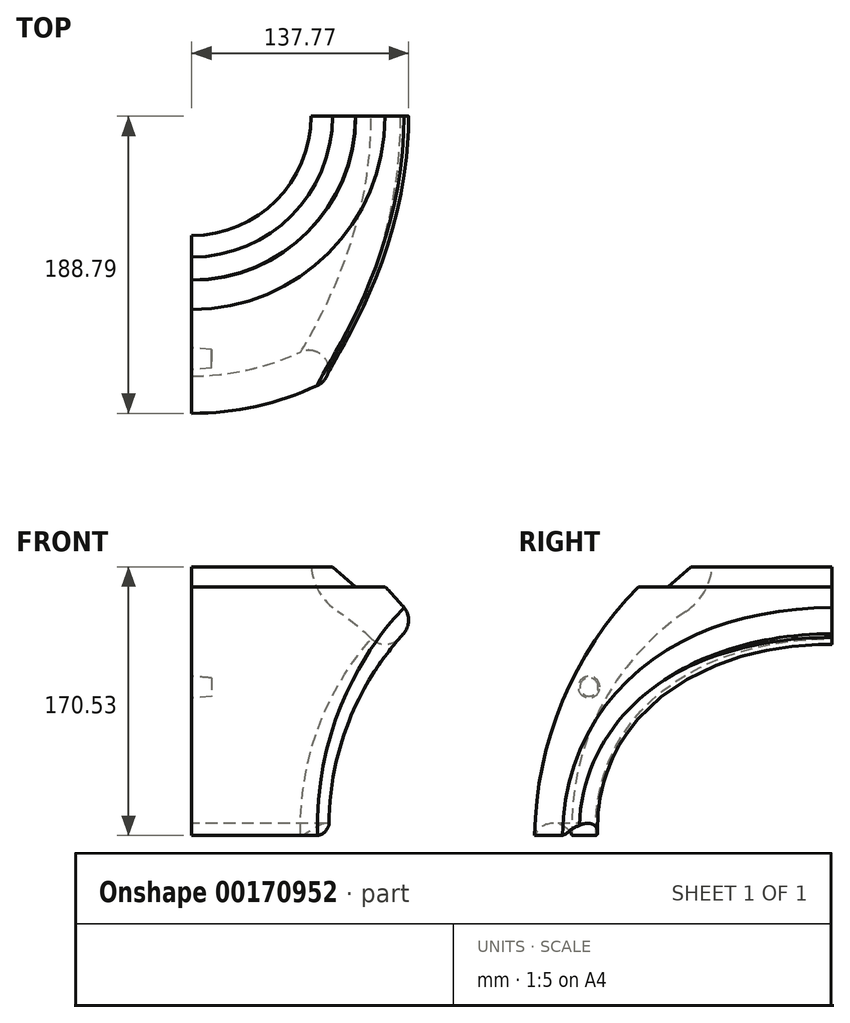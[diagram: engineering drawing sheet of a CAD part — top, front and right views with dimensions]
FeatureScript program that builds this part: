
annotation { "Feature Type Name" : "Feature", "Feature Type Description" : "" }
export const myFeature = defineFeature(function(context is Context, id is Id, definition is map)
    precondition{}
    {
        {
            var Q0;
            Q0=qCreatedBy(makeId("Front.planeOp"),FACE);
            var sketch = newSketch(context, id + "F0", { "sketchPlane" : qUnion([Q0])});
            skLineSegment(sketch, "E0", {"start": v(0, -5.54) * mm, "end": v(0, 0) * mm});
            skArc(sketch, "E1", {"start": v(-7.01, 164.95) * mm, "mid": v(-121.1, 112.22) * mm, "end": v(-165, -5.54) * mm});
            skLineSegment(sketch, "E2", {"start": v(-165, -5.54) * mm, "end": v(0, -5.54) * mm});
            skLineSegment(sketch, "E3", {"start": v(-165, -5.54) * mm, "end": v(-165, -5.54) * mm});
            skLineSegment(sketch, "E4", {"start": v(-122.9, 152.25) * mm, "end": v(-122.9, 152.25) * mm});
            skLineSegment(sketch, "E5", {"start": v(-122.9, 152.25) * mm, "end": v(-104.2, 152.25) * mm});
            skLineSegment(sketch, "E6", {"start": v(-89.51, 164.95) * mm, "end": v(-104, 152.25) * mm});
            skLineSegment(sketch, "E7", {"start": v(-104, 152.25) * mm, "end": v(-104.2, 152.25) * mm});
            skArc(sketch, "E8", {"start": v(-188.8, -5.58) * mm, "mid": v(-176.91, 2.06) * mm, "end": v(-165, -5.54) * mm});
            skArc(sketch, "E9", {"start": v(-122.9, 152.25) * mm, "mid": v(-170.99, 79.65) * mm, "end": v(-188.8, -5.58) * mm});
            skLineSegment(sketch, "E10", {"start": v(0.42, 164.95) * mm, "end": v(0, -5.54) * mm});
            skLineSegment(sketch, "E11", {"start": v(0.42, 164.95) * mm, "end": v(-89.51, 164.95) * mm});
            skLineSegment(sketch, "E12", {"start": v(0.42, 164.95) * mm, "end": v(0.42, 190.35) * mm});
            skLineSegment(sketch, "E13", {"start": v(0.42, 190.35) * mm, "end": v(-39.8, 190.35) * mm});
            skArc(sketch, "E14", {"start": v(-82.03, 173.69) * mm, "mid": v(-104.33, 166.51) * mm, "end": v(-122.9, 152.25) * mm});
            skLineSegment(sketch, "E15", {"start": v(-82.03, 173.69) * mm, "end": v(-64.21, 173.69) * mm});
            skLineSegment(sketch, "E16", {"start": v(-64.21, 173.69) * mm, "end": v(-39.8, 190.35) * mm});
            skSolve(sketch);
        }
        {
            var Q0;
            {var subQ2=sQuery(id+"F0.wireOp",EDGE,"E1");Q0=makeQuery(id+"F0.imprint","IMPRINT",FACE,{"disambiguationData":[TD([[makeQuery(id+"F0.imprint","IMPRINT",EDGE,{"derivedFrom":subQ2}),-1.0]])]});}
            var Q1;
            Q1=sQuery(id+"F0.wireOp",EDGE,"E0");
            revolve(context, id + "F1", {"entities" : qUnion([Q0]), "axis" : qUnion([Q1]), "revolveType" : RevolveType.ONE_DIRECTION, "angle" : 90 * degree});
        }
        {
            var Q0;
            Q0=qCreatedBy(makeId("Front.planeOp"),FACE);
            var sketch = newSketch(context, id + "F2", { "sketchPlane" : qUnion([Q0])});
            skCircle(sketch, "E17", {"center": v(-269.33, 0) * mm, "radius": 182.15 * mm});
            skSolve(sketch);
        }
        {
            var Q0;
            Q0=makeQuery(id+"F2.imprint","IMPRINT",FACE,{"disambiguationData":[TD([[makeQuery(id+"F2.imprint","IMPRINT",EDGE,{"derivedFrom":sQuery(id+"F2.wireOp",EDGE,"E17")}),1.0]])]});
            extrude(context, id + "F3", {"entities" : qUnion([Q0]), "operationType" : NewBodyOperationType.REMOVE, "endBound" : BoundingType.THROUGH_ALL, "depth" : 25.4 * mm});
        }
        {
            var Q0;
            Q0=makeQuery(id+"F3.boolean.opBoolean","INTERSECT",EDGE,{"derivedFrom":[makeQuery(id+"F1.opRevolve","SWEPT_FACE",FACE,{"disambiguationData":[OSD([sQuery(id+"F0.wireOp",EDGE,"E1")])]}),makeQuery(id+"F3.opExtrude","SWEPT_FACE",FACE,{"disambiguationData":[OSD([sQuery(id+"F2.wireOp",EDGE,"E17")])]})]});
            fillet(context, id + "F4", {"entities" : qUnion([Q0]), "radius" : 12.7 * mm, "tangentPropagation" : true, "allowEdgeOverflow" : false});
        }
        {
            var Q0;
            Q0=makeQuery(id+"F1.opRevolve","SWEPT_BODY",BODY,{"disambiguationData":[OSD([sQuery(id+"F0.wireOp",EDGE,"P5tG0YWO-6deF-1cme-UMVW-zcR6kJzPuuW9"),sQuery(id+"F0.wireOp",EDGE,"l9n6v4p5-8KPe-az1E-jcck-v7UenKci9iHe"),sQuery(id+"F0.wireOp",EDGE,"E1"),sQuery(id+"F0.wireOp",EDGE,"pzOhoHtW-SofR-Ddh6-lOb0-XZiDlA6Nqesa"),sQuery(id+"F0.wireOp",EDGE,"BmCeMnuf-rN2F-0dpX-TeqH-BNhEuHFPvOd4"),sQuery(id+"F0.wireOp",EDGE,"7X3JqiTL-AP0i-cL5I-gk5P-m7c9Aaf5Bweu")])]});
            var Q1;
            Q1=qCreatedBy(makeId("Right.planeOp"),FACE);
            mirror(context, id + "F5", {"operationType" : NewBodyOperationType.ADD, "entities" : qUnion([Q0]), "mirrorPlane" : qUnion([Q1])});
        }
        {
            var Q0;
            Q0=qCreatedBy(makeId("Front.planeOp"),FACE);
            var sketch = newSketch(context, id + "F6", { "sketchPlane" : qUnion([Q0])});
            skLineSegment(sketch, "E18.bottom", {"start": v(-157.26, 192.18) * mm, "end": v(0, 192.18) * mm});
            skLineSegment(sketch, "E18.top", {"start": v(-157.26, -9.94) * mm, "end": v(0, -9.94) * mm});
            skLineSegment(sketch, "E18.left", {"start": v(-157.26, 192.18) * mm, "end": v(-157.26, -9.94) * mm});
            skLineSegment(sketch, "E18.right", {"start": v(0, 192.18) * mm, "end": v(0, -9.94) * mm});
            skSolve(sketch);
        }
        {
            var Q0;
            Q0=makeQuery(id+"F5.opPattern","COPY",EDGE,{"derivedFrom":makeQuery(id+"F3.boolean.opBoolean","INTERSECT",EDGE,{"derivedFrom":[makeQuery(id+"F1.opRevolve","SWEPT_FACE",FACE,{"disambiguationData":[OSD([sQuery(id+"F0.wireOp",EDGE,"E9")])]}),makeQuery(id+"F3.opExtrude","SWEPT_FACE",FACE,{"disambiguationData":[OSD([sQuery(id+"F2.wireOp",EDGE,"E17")])]})]}),"instanceName":"1"});
            fillet(context, id + "F7", {"entities" : qUnion([Q0]), "radius" : 12.7 * mm, "tangentPropagation" : true, "allowEdgeOverflow" : false});
        }
        {
            var Q0;
            Q0 = qSketchRegion(id + "F6", true);
            extrude(context, id + "F8", {"entities" : qUnion([Q0]), "operationType" : NewBodyOperationType.REMOVE, "endBound" : BoundingType.THROUGH_ALL, "depth" : 25.4 * mm});
        }
        {
            var Q0;
            {var subQ0=makeQuery(id+"F1.opRevolve","SWEPT_FACE",FACE,{"disambiguationData":[OSD([sQuery(id+"F0.wireOp",EDGE,"E11")])]});Q0=makeQuery(id+"F5.boolean.opBoolean","MERGE",FACE,{"derivedFrom":[subQ0,makeQuery(id+"F5.opPattern","COPY",FACE,{"derivedFrom":subQ0,"instanceName":"1"})]});}
            var sketch = newSketch(context, id + "F9", { "sketchPlane" : qUnion([Q0])});
            skCircle(sketch, "E19", {"center": v(0, 0) * mm, "radius": 75.9 * mm});
            skSolve(sketch);
        }
        {
            var Q0;
            Q0 = qSketchRegion(id + "F9", true);
            extrude(context, id + "F10", {"entities" : qUnion([Q0]), "operationType" : NewBodyOperationType.REMOVE, "endBound" : BoundingType.THROUGH_ALL, "oppositeDirection" : true, "depth" : 25.4 * mm});
        }
        {
            var Q0;
            {var subQ0=makeQuery(id+"F1.opRevolve","SWEPT_FACE",FACE,{"disambiguationData":[OSD([sQuery(id+"F0.wireOp",EDGE,"E1")])]});Q0=makeQuery(id+"F10.boolean.opBoolean","INTERSECT",EDGE,{"derivedFrom":[makeQuery(id+"F5.boolean.opBoolean","MERGE",FACE,{"derivedFrom":[subQ0,makeQuery(id+"F5.opPattern","COPY",FACE,{"derivedFrom":subQ0,"instanceName":"1"})]}),makeQuery(id+"F10.opExtrude","SWEPT_FACE",FACE,{"disambiguationData":[OSD([sQuery(id+"F9.wireOp",EDGE,"E19")])]})]});}
            fillet(context, id + "F11", {"entities" : qUnion([Q0]), "radius" : 38.1 * mm, "tangentPropagation" : true, "allowEdgeOverflow" : false});
        }
        {
            var Q0;
            Q0=makeQuery(id+"F8.boolean.opBoolean","COPY",FACE,{"derivedFrom":makeQuery(id+"F8.opExtrude","SWEPT_FACE",FACE,{"disambiguationData":[OSD([sQuery(id+"F6.wireOp",EDGE,"E18.right")])]})});
            var sketch = newSketch(context, id + "F12", { "sketchPlane" : qUnion([Q0])});
            skCircle(sketch, "E20", {"center": v(154.16, 88.6) * mm, "radius": 6.9 * mm});
            skSolve(sketch);
        }
        {
            var Q0;
            Q0 = qSketchRegion(id + "F12", true);
            extrude(context, id + "F13", {"entities" : qUnion([Q0]), "operationType" : NewBodyOperationType.REMOVE, "oppositeDirection" : true, "depth" : 12.7 * mm, "hasDraft" : true, "draftAngle" : 5 * degree, "draftPullDirection" : true});
        }
    });
